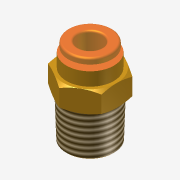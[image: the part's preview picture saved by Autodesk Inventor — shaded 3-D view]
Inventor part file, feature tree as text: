
AUTODESK INVENTOR PART (.ipt)
format: ipt  version: unknown  size: 241,664 bytes
history: native  units: mm
features: imported_body x1, thread x1
ambient origin geometry x8: Origin, YZ Plane, XZ Plane, XY Plane, X Axis, Y Axis, Z Axis, Center Point
feature tree (2):
  imported_body  "Base1"
  thread  "Thread2"  [1 undecoded]
note: 1 required parameter value undecoded (feature->parameter linkage not recoverable at this tier; creation-order binding heuristic only, values carry confidence <= 0.55)
